# Revit family: CBCGTYP004
name_source: partatom
category: Furniture
units: mm (PartAtom-declared; Revit-internal decimal feet)

## family parameters
Always vertical = Yes
Cut with Voids When Loaded = No
OmniClass Number = 23.40.20.00
OmniClass Title = General Furniture and Specialties
Render Appearance Source = Family Geometry
Room Calculation Point = No
Shared = No
Work Plane-Based = No

## types (1)
- CBCGTYP004
    Cost = 6584 $
    Default Elevation = 0 mm  [stored 0 ft]
    Description = 1 x Cbx Partial Depth Bbf Ped 23dx28hx16w, 1 x CB Desk Return RH 24Dx48Wx29H, 1 x Cb Desk Shell Full Mod Recessed 36dx72wx29h, 1 x Cbx Partial Depth Ff Ped 23dx28hx16w
    Exported From CET Designer = Yes
    Manufacturer = AIS
    Model = X-BBFPFS23
    Show CBCGTYP004 = Yes
    VisibilityIndex = 0

note: [stored X ft] marks values corroborated as IEEE doubles in the binary element streams (Revit-internal decimal feet)

## geometry (parser evidence)
native form markers: Sweep x3
no freeform markers — native parametric forms only
